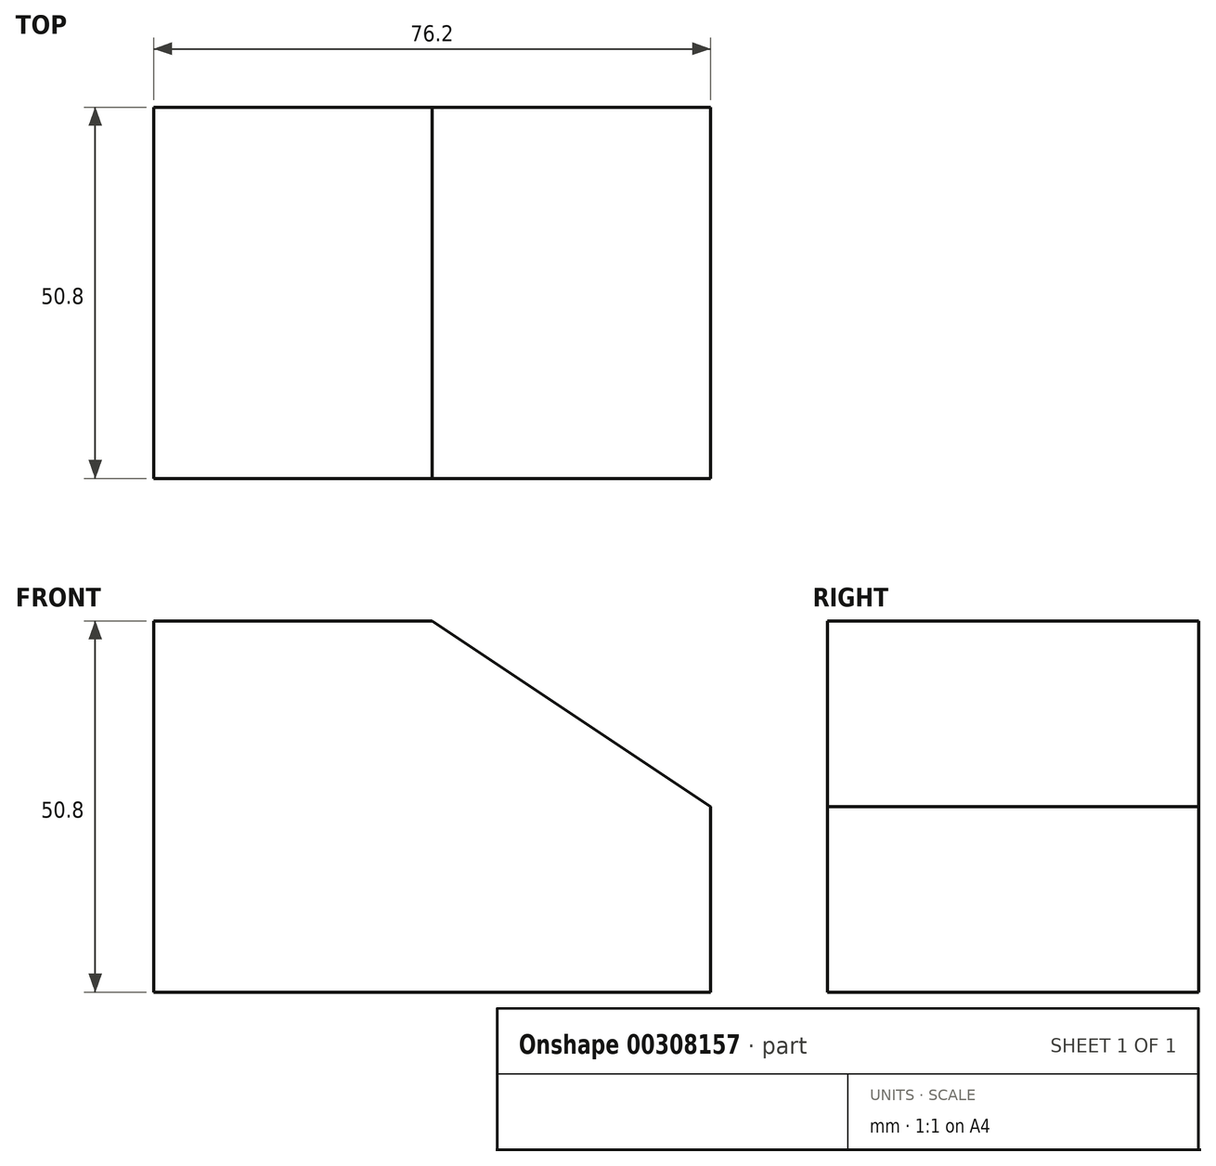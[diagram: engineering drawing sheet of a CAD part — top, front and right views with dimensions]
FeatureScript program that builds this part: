
annotation { "Feature Type Name" : "Feature", "Feature Type Description" : "" }
export const myFeature = defineFeature(function(context is Context, id is Id, definition is map)
    precondition{}
    {
        {
            var Q0;
            Q0=qCreatedBy(makeId("Front.planeOp"),FACE);
            var sketch = newSketch(context, id + "F0", { "sketchPlane" : qUnion([Q0])});
            skLineSegment(sketch, "E0", {"start": v(-52.28, 36.4) * mm, "end": v(-14.18, 36.4) * mm});
            skLineSegment(sketch, "E1", {"start": v(-52.28, 36.4) * mm, "end": v(-52.28, -14.4) * mm});
            skLineSegment(sketch, "E2", {"start": v(-52.28, -14.4) * mm, "end": v(23.92, -14.4) * mm});
            skLineSegment(sketch, "E3", {"start": v(23.92, -14.4) * mm, "end": v(23.92, 11) * mm});
            skLineSegment(sketch, "E4", {"start": v(-14.18, 36.4) * mm, "end": v(23.92, 11) * mm});
            skSolve(sketch);
        }
        {
            var Q0;
            Q0=makeQuery(id+"F0.imprint","IMPRINT",FACE,{"disambiguationData":[TD([[makeQuery(id+"F0.imprint","IMPRINT",EDGE,{"derivedFrom":sQuery(id+"F0.wireOp",EDGE,"E0")}),-1.0]])]});
            extrude(context, id + "F1", {"entities" : qUnion([Q0]), "oppositeDirection" : true, "depth" : 50.8 * mm});
        }
    });
